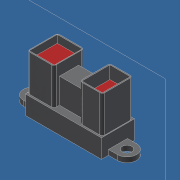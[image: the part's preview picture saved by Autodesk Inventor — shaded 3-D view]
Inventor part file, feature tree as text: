
AUTODESK INVENTOR PART (.ipt)
format: ipt  version: 2016 SP2 (Build 200236200, 236)  size: 488,960 bytes
history: native  units: mm
features: sketch x18, extrude x15, other x3, fillet x2
ambient origin geometry x8: Origin, YZ Plane, XZ Plane, XY Plane, X Axis, Y Axis, Z Axis, Center Point
bodies: Solid1 (feature_tree)
feature tree (38):
  sketch  "Sketch1"  dims[d0=37.0mm d1=13.0mm]
  extrude  "Extrusion1"  Depth=13.0mm
  extrude  "Extrusion2"  Depth=3.75mm
  extrude  "Extrusion3"  Depth=2.0mm TaperAngle=0.0deg
  extrude  "Extrusion4"  Depth=29.9mm
  extrude  "Extrusion5"  Depth=13.0mm
  extrude  "Extrusion6"  Depth=14.4mm
  extrude  "Extrusion7"  Depth=4.5mm TaperAngle=0.0deg
  extrude  "Extrusion8"  Depth=2.2mm TaperAngle=0.0deg
  extrude  "Extrusion9"  Depth=0.014mm TaperAngle=0.0deg
  extrude  "Extrusion10"  Depth=11.0mm
  extrude  "Extrusion11"  Depth=8.0mm
  sketch  "Sketch14"  dims[d142=5.05mm d143=10.1mm]
  extrude  "Extrusion12"  Depth=5.0mm TaperAngle=0.0deg
  extrude  "Extrusion13"  Depth=10.1mm
  extrude  "Extrusion14"  Depth=2.0mm TaperAngle=0.0deg
  sketch  "Sketch18"  dims[d154=4.0mm d155=0.0mm]
  extrude  "Extrusion15"  Depth=9.9mm TaperAngle=0.0deg
  fillet  "Fillet1"  Radius=29.0mm
  fillet  "Fillet2"  Radius=12.0mm
  sketch  "Sketch2"  dims[d30=3.75mm d31=3.75mm]
  other  "Image1"
  sketch  "Sketch3"  dims[d32=29.5mm d33=2.0mm d34=0.0mm]
  other  "Image3"
  sketch  "Sketch4"  dims[d46=14.95mm d48=29.9mm]
  other  "Image4"
  sketch  "Sketch6"  dims[d49=13.0mm d50=0.0mm d78=14.75mm]
  sketch  "Sketch7"  dims[d79=29.5mm d80=14.4mm]
  sketch  "Sketch8"  dims[d81=11.9mm d82=0.0mm d124=4.5mm d125=0.0mm]
  sketch  "Sketch9"  dims[d126=2.2mm d127=0.0mm d128=2.2mm d129=0.0mm]
  sketch  "Sketch10"  dims[d130=1.514mm d131=0.0mm d132=0.014mm d133=0.0mm]
  sketch  "Sketch11"  dims[d134=9.8mm d135=11.0mm]
  sketch  "Sketch12"  dims[d136=3.0mm d137=0.0mm d138=8.0mm]
  sketch  "Sketch13"  dims[d139=11.0mm d140=5.0mm d141=0.0mm]
  sketch  "Sketch15"  dims[d144=1.0mm d145=2.0mm d146=0.0mm]
  sketch  "Sketch16"  dims[d147=1.0mm d148=9.9mm d149=0.0mm d150=29.0mm d151=12.0mm]
  sketch  "Sketch17"  dims[d152=2.0mm d153=0.0mm]
  sketch  "Sketch19"  dims[d156=6.0mm d157=7.0mm d158=0.0mm d159=0.8mm d160=1.0mm]
